# Revit family: 3M_Pressure Reducing Control Valve_UNIVAL_UPRV-0301 - 50-200 mm
name_source: partatom
category: Pipe Accessories
revit_build: Autodesk Revit 2016 (Build: 20150220_1215(x64)
units: mm (PartAtom-declared; Revit-internal decimal feet)

## family parameters
Always vertical = Yes
Cut with Voids When Loaded = No
OmniClass Number = 23.65.55.14
OmniClass Title = Valves for Liquid Services
Part Type = Valve - Breaks Into
Round Connector Dimension = Use Diameter
Shared = No
Work Plane-Based = No

## types (7) — shared parameters
Body Material = Ductile iron
Certifications = CE
Color = UNIVAL_Red
Connection Type = Flanged / Grooved
Description = Pressure reducing control valve
Description TR = Basınç düşürücü kontrol vanası
Disc Material = EPDM coated ductile iron
Loss Method = Not Defined
Manufacturer = Giacomini Unival
Giacomini Unival
Giacomini Unival
Max. Working Temperature = 90°C
Pressure Rating = PN16 / PN25
URL = http://www.unival.com.tr

## per-type parameters (varying)
| type | D | DN | Elbow_D | Elbow_curve | Elbow_dist | Elbow_h | Ext_dist | Flange | Flange_w | Flange_wMinus | H | H1 | Hexagon_d | Hexagon_h | Kv | L | Model | Profile2_x | Profile_d | Profile_y | Top_D |
| DN50 | 165 mm | 50 mm | 64 mm  [stored 0.209974 ft] | 120 mm | 93 mm  [stored 0.305118 ft] | 60 mm  [stored 0.19685 ft] | 5 mm  [stored 0.0164042 ft] | M_Flange - 15-450 mm : DN50 | 17 mm | -17 mm | 150 mm | 68 mm | 63 mm  [stored 0.206693 ft] | 15 mm  [stored 0.0492126 ft] | 88 | 220 mm | UPRV-0301X050 | 73 mm  [stored 0.239501 ft] | 24 mm  [stored 0.0787402 ft] | 50 mm  [stored 0.164042 ft] | 32 mm  [stored 0.104987 ft] |
| DN65 | 185 mm | 65 mm | 65 mm  [stored 0.213255 ft] | 116 mm  [stored 0.380577 ft] | 93 mm  [stored 0.305118 ft] | 58 mm  [stored 0.190289 ft] | 5 mm  [stored 0.0164042 ft] | M_Flange - 15-450 mm : DN65 | 17 mm | -17 mm | 155 mm | 63 mm  [stored 0.206693 ft] | 66 mm  [stored 0.216535 ft] | 15 mm  [stored 0.0492126 ft] | 88 | 220 mm | UPRV-0301X065 | 73 mm  [stored 0.239501 ft] | 31 mm | 55 mm  [stored 0.180446 ft] | 33 mm  [stored 0.108268 ft] |
| DN80 | 200 mm | 80 mm | 80 mm  [stored 0.262467 ft] | 130 mm | 125 mm | 65 mm  [stored 0.213255 ft] | 33 mm  [stored 0.108268 ft] | M_Flange - 15-450 mm : DN80 | 17 mm | -17 mm | 172 mm | 72 mm  [stored 0.23622 ft] | 80 mm  [stored 0.262467 ft] | 15 mm  [stored 0.0492126 ft] | 174 | 283 mm | UPRV-0301X080 | 94 mm  [stored 0.308399 ft] | 38 mm  [stored 0.124672 ft] | 62 mm  [stored 0.203412 ft] | 40 mm  [stored 0.131234 ft] |
| DN100 | 220 mm | 100 mm | 100 mm  [stored 0.328084 ft] | 130 mm | 151 mm | 65 mm  [stored 0.213255 ft] | 40 mm  [stored 0.131234 ft] | M_Flange - 15-450 mm : DN100 | 17 mm | -17 mm | 180 mm | 70 mm  [stored 0.229659 ft] | 100 mm  [stored 0.328084 ft] | 15 mm  [stored 0.0492126 ft] | 187 | 335 mm | UPRV-0301X100 | 112 mm | 48 mm  [stored 0.15748 ft] | 70 mm  [stored 0.229659 ft] | 50 mm  [stored 0.164042 ft] |
| DN125 | 250 mm | 125 mm | 125 mm | 130 mm | 169 mm | 65 mm  [stored 0.213255 ft] | 42 mm  [stored 0.137795 ft] | M_Flange - 15-450 mm : DN125 | 17 mm | -17 mm | 200 mm | 75 mm | 120 mm | 15 mm  [stored 0.0492126 ft] | 187 | 372 mm | UPRV-0301X125 | 124 mm | 60 mm  [stored 0.19685 ft] | 86 mm  [stored 0.282152 ft] | 60 mm  [stored 0.19685 ft] |
| DN150 | 285 mm | 150 mm | 150 mm | 295 mm | 181 mm | 148 mm | 5 mm  [stored 0.0164042 ft] | M_Flange - 15-450 mm : DN150 | 17 mm | -17 mm | 305 mm | 163 mm | 110 mm  [stored 0.360892 ft] | 30 mm  [stored 0.0984252 ft] | 419 | 395 mm | UPRV-0301X150 | 132 mm | 72 mm  [stored 0.23622 ft] | 100 mm  [stored 0.328084 ft] | 55 mm  [stored 0.180446 ft] |
| DN200 | 340 mm | 200 mm | 200 mm | 400 mm | 212 mm | 200 mm | 6 mm  [stored 0.019685 ft] | M_Flange - 15-450 mm : DN200 | 18 mm  [stored 0.0590551 ft] | -18 mm  [stored -0.0590551 ft] | 383 mm | 213 mm | 130 mm | 30 mm  [stored 0.0984252 ft] | 1139 | 460 mm | UPRV-0301X200 | 153 mm | 96 mm  [stored 0.314961 ft] | 114 mm  [stored 0.374016 ft] | 65 mm  [stored 0.213255 ft] |

note: [stored X ft] marks values corroborated as IEEE doubles in the binary element streams (Revit-internal decimal feet)

## geometry (parser evidence)
native form markers: Sweep x5
no freeform markers — native parametric forms only
